MODEL slx_0b62965fec34
KIND model
CONFIG AbsTol = auto
CONFIG EnableMultiTasking = off
CONFIG FixedStep = 5e-6
CONFIG MaxStep = auto
CONFIG MinStep = auto
CONFIG RelTol = 1e-3
CONFIG SampleTimeConstraint = Unconstrained
CONFIG Solver = FixedStepDiscrete
CONFIG SolverName = FixedStepDiscrete
CONFIG StartTime = 0.0
CONFIG StopTime = 5.0
BLOCK [Reference] AC DC Converter Rectifier  REF=powerlib/Power
Electronics/Universal Bridge
  Ports = [0, 0, 0, 0, 0, 3, 2]
  SourceBlock = powerlib/Power\nElectronics/Universal Bridge
  SourceProductBaseCode = PS
  SourceProductName = Simscape Power Systems
  SourceType = Universal Bridge
BLOCK [Sum] Add
  InputSameDT = off
  Inputs = +-
  OutDataTypeStr = Inherit: Inherit via internal rule
  Ports = [2, 1]
  SaturateOnIntegerOverflow = off
BLOCK [Sum] Add1
  InputSameDT = off
  Inputs = +-
  OutDataTypeStr = Inherit: Inherit via internal rule
  Ports = [2, 1]
  SaturateOnIntegerOverflow = off
BLOCK [Sum] Add2
  InputSameDT = off
  Inputs = +-
  OutDataTypeStr = Inherit: Inherit via internal rule
  Ports = [2, 1]
  SaturateOnIntegerOverflow = off
BLOCK [Reference] Battery  REF=electricdrivelib/Extra Sources/Battery
  Ports = [0, 1, 0, 0, 0, 2]
  SourceBlock = electricdrivelib/Extra Sources/Battery
  SourceProductBaseCode = PS
  SourceProductName = Simscape Power Systems
  SourceType = Battery
BLOCK [BusSelector] Bus Selector
  OutputAsBus = off
  OutputSignals = SOC (%),Current (A),Voltage (V)
  Ports = [1, 3]
BLOCK [BusSelector] Bus Selector1
  OutputAsBus = off
  OutputSignals = V_PV,I_PV
  Ports = [1, 2]
BLOCK [Constant] Constant
  Value = 25.98
BLOCK [Constant] Constant1
  Value = 100
BLOCK [Constant] Constant2
BLOCK [Constant] Constant3
  Value = 0.5
BLOCK [Constant] Constant4
  Value = 1.2
BLOCK [Constant] Constant5
  Value = 0
BLOCK [Constant] Constant6
  Value = 0
BLOCK [Constant] Constant8
  Value = 0
BLOCK [Reference] Current Measurement1  REF=powerlib/Measurements/Current Measurement
  Ports = [0, 1, 0, 0, 0, 1, 1]
  SourceBlock = powerlib/Measurements/Current Measurement
  SourceProductBaseCode = PS
  SourceProductName = Simscape Power Systems
  SourceType = Current Measurement
  UserDataPersistent = on
BLOCK [Reference] Current PID Controller1  REF=simulink/Continuous/PID Controller
  Ports = [1, 1]
  SourceBlock = simulink/Continuous/PID Controller
  SourceProductBaseCode = SL
  SourceProductName = Simulink
  SourceType = PID 1dof
BLOCK [Reference] Current PID Controller2  REF=simulink/Continuous/PID Controller
  Ports = [1, 1]
  SourceBlock = simulink/Continuous/PID Controller
  SourceProductBaseCode = SL
  SourceProductName = Simulink
  SourceType = PID 1dof
BLOCK [Reference] Diode  REF=powerlib/Power
Electronics/Diode
  Ports = [0, 0, 0, 0, 0, 1, 1]
  SourceBlock = powerlib/Power\nElectronics/Diode
  SourceProductBaseCode = PS
  SourceProductName = Simscape Power Systems
  SourceType = Diode
BLOCK [Display] Display
  Decimation = 1
  Ports = [1]
BLOCK [Display] Display1
  Decimation = 1
  Ports = [1]
BLOCK [Display] Display2
  Decimation = 1
  Ports = [1]
BLOCK [Display] Display3
  Decimation = 1
  Ports = [1]
BLOCK [Display] Display4
  Decimation = 1
  Ports = [1]
BLOCK [Display] Display5
  Decimation = 1
  Ports = [1]
BLOCK [Display] Display6
  Decimation = 1
  Ports = [1]
BLOCK [Reference] Filter  REF=powerlib/Elements/Series RLC Branch
  Ports = [0, 0, 0, 0, 0, 1, 1]
  SourceBlock = powerlib/Elements/Series RLC Branch
  SourceProductBaseCode = PS
  SourceProductName = Simscape Power Systems
  SourceType = Series RLC Branch
BLOCK [From] From
  GotoTag = S_P
BLOCK [From] From1
  GotoTag = S_N
BLOCK [From] From10
  GotoTag = Ib_ref
BLOCK [From] From11
  GotoTag = V_bus
  TagVisibility = global
BLOCK [From] From12
  GotoTag = Ib_ref_dis
BLOCK [From] From13
  GotoTag = Bt_sg
  TagVisibility = global
BLOCK [From] From14
  GotoTag = S_boost
BLOCK [From] From15
  GotoTag = V_pv
  TagVisibility = global
BLOCK [From] From16
  GotoTag = V_bus
  TagVisibility = global
BLOCK [From] From17
  GotoTag = Irradiance
  TagVisibility = global
BLOCK [From] From18
  GotoTag = I_bus
  TagVisibility = global
BLOCK [From] From19
  GotoTag = V_Grid
  TagVisibility = global
BLOCK [From] From2
  GotoTag = I_b
  TagVisibility = global
BLOCK [From] From20
  GotoTag = P_bus
  TagVisibility = global
BLOCK [From] From21
  GotoTag = P_pv
  TagVisibility = global
BLOCK [From] From22
  GotoTag = Irradiance
  TagVisibility = global
BLOCK [From] From23
  GotoTag = Solar
  TagVisibility = global
BLOCK [From] From24
  GotoTag = Solar_v
  TagVisibility = global
BLOCK [From] From25
  GotoTag = Wind
BLOCK [From] From26
  GotoTag = Wind_V
BLOCK [From] From27
  GotoTag = Grid_V
BLOCK [From] From3
  GotoTag = SOC
  TagVisibility = global
BLOCK [From] From4
  GotoTag = I_pv
  TagVisibility = global
BLOCK [From] From5
  GotoTag = Ib_ref_ch
BLOCK [From] From6
  GotoTag = Wind_Speed
BLOCK [From] From7
  GotoTag = I_bus
  TagVisibility = global
BLOCK [From] From8
  GotoTag = V_b
  TagVisibility = global
BLOCK [From] From9
  GotoTag = V_bus
  TagVisibility = global
BLOCK [Gain] Gain
  Gain = -1
  OutDataTypeStr = Inherit: Inherit via internal rule
  ParamDataTypeStr = Inherit: Inherit via internal rule
  SaturateOnIntegerOverflow = off
BLOCK [Goto] Goto
  GotoTag = SOC
  TagVisibility = global
BLOCK [Goto] Goto1
  GotoTag = I_b
  TagVisibility = global
BLOCK [Goto] Goto10
  GotoTag = V_pv
  TagVisibility = global
BLOCK [Goto] Goto11
  GotoTag = I_pv
  TagVisibility = global
BLOCK [Goto] Goto12
  GotoTag = Irradiance
  TagVisibility = global
BLOCK [Goto] Goto13
  GotoTag = S_boost
BLOCK [Goto] Goto14
  GotoTag = V_bus
  TagVisibility = global
BLOCK [Goto] Goto15
  GotoTag = I_bus
  TagVisibility = global
BLOCK [Goto] Goto16
  GotoTag = gridsg
BLOCK [Goto] Goto17
  GotoTag = P_bus
  TagVisibility = global
BLOCK [Goto] Goto18
  GotoTag = P_pv
  TagVisibility = global
BLOCK [Goto] Goto19
  GotoTag = Wind_Speed
BLOCK [Goto] Goto2
  GotoTag = V_b
  TagVisibility = global
BLOCK [Goto] Goto20
  GotoTag = Solar
  TagVisibility = global
BLOCK [Goto] Goto21
  GotoTag = Solar_v
  TagVisibility = global
BLOCK [Goto] Goto22
  GotoTag = Wind
BLOCK [Goto] Goto23
  GotoTag = Wind_V
BLOCK [Goto] Goto24
  GotoTag = Grid_V
BLOCK [Goto] Goto3
  GotoTag = S_N
BLOCK [Goto] Goto4
  GotoTag = S_P
BLOCK [Goto] Goto5
  GotoTag = Ib_ref_ch
BLOCK [Goto] Goto6
  GotoTag = V_Grid
  TagVisibility = global
BLOCK [Goto] Goto7
  GotoTag = Ib_ref_dis
BLOCK [Goto] Goto8
  GotoTag = Ib_ref
BLOCK [Goto] Goto9
  GotoTag = Bt_sg
  TagVisibility = global
BLOCK [Reference] Ground  REF=powerlib/Elements/Ground
  Ports = [0, 0, 0, 0, 0, 1]
  SourceBlock = powerlib/Elements/Ground
  SourceProductBaseCode = PS
  SourceProductName = Simscape Power Systems
  SourceType = Ground
BLOCK [Reference] IGBT//Diode  REF=powerlib/Power
Electronics/IGBT//Diode
  Ports = [1, 1, 0, 0, 0, 1, 1]
  SourceBlock = powerlib/Power\nElectronics/IGBT//Diode
  SourceProductBaseCode = PS
  SourceProductName = Simscape Power Systems
  SourceType = IGBT/Diode
BLOCK [Reference] Ideal Switch  REF=powerlib/Power
Electronics/Ideal Switch
  Ports = [1, 0, 0, 0, 0, 1, 1]
  SourceBlock = powerlib/Power\nElectronics/Ideal Switch
  SourceProductBaseCode = PS
  SourceProductName = Simscape Power Systems
  SourceType = Ideal Switch
BLOCK [Logic] Logical Operator
  AllPortsSameDT = off
  Operator = NOT
  OutDataTypeStr = boolean
  Ports = [1, 1]
BLOCK [Reference] Mosfet  REF=powerlib/Power
Electronics/Mosfet
  Ports = [1, 0, 0, 0, 0, 1, 1]
  SourceBlock = powerlib/Power\nElectronics/Mosfet
  SourceProductBaseCode = PS
  SourceProductName = Simscape Power Systems
  SourceType = Mosfet
BLOCK [Reference] Mosfet1  REF=powerlib/Power
Electronics/Mosfet
  Ports = [1, 0, 0, 0, 0, 1, 1]
  SourceBlock = powerlib/Power\nElectronics/Mosfet
  SourceProductBaseCode = PS
  SourceProductName = Simscape Power Systems
  SourceType = Mosfet
BLOCK [Reference] PV Array  REF=re_lib/Solar/PV Array
  Ports = [2, 1, 0, 0, 0, 0, 2]
  SourceBlock = re_lib/Solar/PV Array
  SourceProductBaseCode = PS
  SourceProductName = Simscape Power Systems
  SourceType = PV array
BLOCK [Reference] PWM Generator (DC-DC)  REF=powerlib_meascontrol/Pulse & Signal
Generators/PWM Generator
(DC-DC)
  Ports = [1, 1]
  SourceBlock = powerlib_meascontrol/Pulse & Signal\nGenerators/PWM Generator\n(DC-DC)
  SourceProductBaseCode = PS
  SourceProductName = Simscape Power Systems
  SourceType = PWM Generator (DC-DC)
BLOCK [Reference] PWM Generator (DC-DC)1  REF=powerlib_meascontrol/Pulse & Signal
Generators/PWM Generator
(DC-DC)
  Ports = [1, 1]
  SourceBlock = powerlib_meascontrol/Pulse & Signal\nGenerators/PWM Generator\n(DC-DC)
  SourceProductBaseCode = PS
  SourceProductName = Simscape Power Systems
  SourceType = PWM Generator (DC-DC)
BLOCK [Product] P_bus
  InputSameDT = off
  OutDataTypeStr = Inherit: Inherit via internal rule
  Ports = [2, 1]
  RndMeth = Floor
  SaturateOnIntegerOverflow = off
BLOCK [Product] P_pv
  InputSameDT = off
  OutDataTypeStr = Inherit: Inherit via internal rule
  Ports = [2, 1]
  RndMeth = Floor
  SaturateOnIntegerOverflow = off
BLOCK [Reference] Permanent Magnet Synchronous Machine  REF=powerlib/Machines/Permanent Magnet
Synchronous Machine
  Ports = [1, 1, 0, 0, 0, 3]
  SourceBlock = powerlib/Machines/Permanent Magnet\nSynchronous Machine
  SourceProductBaseCode = PS
  SourceProductName = Simscape Power Systems
  SourceType = Permanent Magnet Synchronous Machine
BLOCK [Scope] Scope
  Floating = off
  NumInputPorts = 8
  Ports = [8]
  ScopeSpecificationString = Simulink.scopes.TimeScopeBlockCfg('CurrentConfiguration', extmgr.ConfigurationSet(extmgr.Configuration('Core','General UI',true,'FigureColor',[1 1 1]),extmgr.Configuration('Core','Source UI',true),extmgr.Configuration('Sources','WiredSimulink',true,'DataLogging',true),extmgr.Configuration('Visuals','Time Domain',true,'SerializedDisplays',{struct('MinYLimReal','-248.28438','MaxYLimReal','248.28537'...<+7768ch>
BLOCK [Reference] Series RLC Branch  REF=powerlib/Elements/Series RLC Branch
  Ports = [0, 0, 0, 0, 0, 1, 1]
  SourceBlock = powerlib/Elements/Series RLC Branch
  SourceProductBaseCode = PS
  SourceProductName = Simscape Power Systems
  SourceType = Series RLC Branch
BLOCK [Reference] Series RLC Branch1  REF=powerlib/Elements/Series RLC Branch
  Ports = [0, 0, 0, 0, 0, 1, 1]
  SourceBlock = powerlib/Elements/Series RLC Branch
  SourceProductBaseCode = PS
  SourceProductName = Simscape Power Systems
  SourceType = Series RLC Branch
BLOCK [Reference] Series RLC Branch2  REF=powerlib/Elements/Series RLC Branch
  Ports = [0, 0, 0, 0, 0, 1, 1]
  SourceBlock = powerlib/Elements/Series RLC Branch
  SourceProductBaseCode = PS
  SourceProductName = Simscape Power Systems
  SourceType = Series RLC Branch
BLOCK [Reference] Series RLC Branch3  REF=powerlib/Elements/Series RLC Branch
  Ports = [0, 0, 0, 0, 0, 1, 1]
  SourceBlock = powerlib/Elements/Series RLC Branch
  SourceProductBaseCode = PS
  SourceProductName = Simscape Power Systems
  SourceType = Series RLC Branch
BLOCK [Reference] Series RLC Branch4  REF=powerlib/Elements/Series RLC Branch
  Ports = [0, 0, 0, 0, 0, 1, 1]
  SourceBlock = powerlib/Elements/Series RLC Branch
  SourceProductBaseCode = PS
  SourceProductName = Simscape Power Systems
  SourceType = Series RLC Branch
BLOCK [Reference] Series RLC Branch5  REF=powerlib/Elements/Series RLC Branch
  Ports = [0, 0, 0, 0, 0, 1, 1]
  SourceBlock = powerlib/Elements/Series RLC Branch
  SourceProductBaseCode = PS
  SourceProductName = Simscape Power Systems
  SourceType = Series RLC Branch
BLOCK [Reference] Series RLC Branch6  REF=powerlib/Elements/Series RLC Branch
  Ports = [0, 0, 0, 0, 0, 1, 1]
  SourceBlock = powerlib/Elements/Series RLC Branch
  SourceProductBaseCode = PS
  SourceProductName = Simscape Power Systems
  SourceType = Series RLC Branch
BLOCK [Reference] Series RLC Branch7  REF=powerlib/Elements/Series RLC Branch
  Ports = [0, 0, 0, 0, 0, 1, 1]
  SourceBlock = powerlib/Elements/Series RLC Branch
  SourceProductBaseCode = PS
  SourceProductName = Simscape Power Systems
  SourceType = Series RLC Branch
BLOCK [Reference] Series RLC Branch8  REF=powerlib/Elements/Series RLC Branch
  Ports = [0, 0, 0, 0, 0, 1, 1]
  SourceBlock = powerlib/Elements/Series RLC Branch
  SourceProductBaseCode = PS
  SourceProductName = Simscape Power Systems
  SourceType = Series RLC Branch
BLOCK [Reference] Series RLC Branch9  REF=powerlib/Elements/Series RLC Branch
  Ports = [0, 0, 0, 0, 0, 1, 1]
  SourceBlock = powerlib/Elements/Series RLC Branch
  SourceProductBaseCode = PS
  SourceProductName = Simscape Power Systems
  SourceType = Series RLC Branch
BLOCK [Step] Step
  After = 0
  Before = 1000
  SampleTime = 0
  Time = 3
BLOCK [Step] Step1
  After = 0
  Before = 12
  SampleTime = 0
  Time = 4
BLOCK [Step] Step2
  After = 0
  Before = 1
  SampleTime = 0
  Time = 1.5
BLOCK [Sum] Sum
  IconShape = round
  InputSameDT = off
  Inputs = |++
  OutDataTypeStr = Inherit: Inherit via internal rule
  Ports = [2, 1]
  SaturateOnIntegerOverflow = off
BLOCK [Switch] Switch
  Criteria = u2 > Threshold
  InputSameDT = off
  SaturateOnIntegerOverflow = off
BLOCK [Switch] Switch1
  Criteria = u2 > Threshold
  InputSameDT = off
  SaturateOnIntegerOverflow = off
BLOCK [Switch] Switch2
  Criteria = u2 ~= 0
  InputSameDT = off
  SaturateOnIntegerOverflow = off
BLOCK [Constant] Temp
  Value = 25
BLOCK [Reference] Three-Phase Breaker  REF=powerlib/Elements/Three-Phase Breaker
  Ports = [1, 0, 0, 0, 0, 3, 3]
  SourceBlock = powerlib/Elements/Three-Phase Breaker
  SourceProductBaseCode = PS
  SourceProductName = Simscape Power Systems
  SourceType = Three-Phase Breaker
BLOCK [Reference] Three-Phase Source 11kv  REF=powerlib/Electrical
Sources/Three-Phase Source
  Ports = [0, 0, 0, 0, 0, 0, 3]
  SourceBlock = powerlib/Electrical\nSources/Three-Phase Source
  SourceProductBaseCode = PS
  SourceProductName = Simscape Power Systems
  SourceType = Three-Phase Source
BLOCK [Reference] Three-Phase Transformer (Two Windings) 11kv//250v 100KVA  REF=powerlib/Elements/Three-Phase
Transformer
(Two Windings)
  Ports = [0, 0, 0, 0, 0, 3, 4]
  SourceBlock = powerlib/Elements/Three-Phase\nTransformer\n(Two Windings)
  SourceProductBaseCode = PS
  SourceProductName = Simscape Power Systems
  SourceType = Three-Phase Transformer (Two Windings)
BLOCK [Reference] Three-Phase V-I Measurement  REF=powerlib/Measurements/Three-Phase
V-I Measurement
  Ports = [0, 0, 0, 0, 0, 3, 3]
  SourceBlock = powerlib/Measurements/Three-Phase\nV-I Measurement
  SourceProductBaseCode = PS
  SourceProductName = Simscape Power Systems
  SourceType = Three-Phase VI Measurement
BLOCK [Reference] Three-Phase V-I Measurement1  REF=powerlib/Measurements/Three-Phase
V-I Measurement
  Ports = [0, 1, 0, 0, 0, 3, 3]
  SourceBlock = powerlib/Measurements/Three-Phase\nV-I Measurement
  SourceProductBaseCode = PS
  SourceProductName = Simscape Power Systems
  SourceType = Three-Phase VI Measurement
BLOCK [Reference] Universal Bridge1  REF=powerlib/Power
Electronics/Universal Bridge
  Ports = [0, 0, 0, 0, 0, 3, 2]
  SourceBlock = powerlib/Power\nElectronics/Universal Bridge
  SourceProductBaseCode = PS
  SourceProductName = Simscape Power Systems
  SourceType = Universal Bridge
BLOCK [Reference] Voltage Measurement2  REF=powerlib/Measurements/Voltage Measurement
  Ports = [0, 1, 0, 0, 0, 2]
  SourceBlock = powerlib/Measurements/Voltage Measurement
  SourceProductBaseCode = PS
  SourceProductName = Simscape Power Systems
  SourceType = Voltage Measurement
  UserDataPersistent = on
BLOCK [Reference] Voltage PID Controller  REF=simulink/Continuous/PID Controller
  Ports = [1, 1]
  SourceBlock = simulink/Continuous/PID Controller
  SourceProductBaseCode = SL
  SourceProductName = Simulink
  SourceType = PID 1dof
BLOCK [Reference] Wind Turbine  REF=re_lib/Wind Generation/Wind Turbine
  Ports = [3, 1]
  SourceBlock = re_lib/Wind Generation/Wind Turbine
  SourceProductBaseCode = PS
  SourceProductName = Simscape Power Systems
  SourceType = Wind Turbine
BLOCK [From] grid
  GotoTag = gridsg
BLOCK [From] grid1
  GotoTag = gridsg
BLOCK [Reference] powergui  REF=powerlib/powergui
  Ports = []
  Priority = 1
  SourceBlock = powerlib/powergui
  SourceProductBaseCode = PS
  SourceProductName = Simscape Power Systems
  SourceType = PSB option menu block
ANNOTATION (root): MEASUREMENT BLOCK
ANNOTATION (root): DESIGNED BY: Er.DANISH NAZIR SHAH <email> 9018561666
ANNOTATION (root): CONTROL BLOCK
ANNOTATION (root): DESIGN OF DC MICROGRID
ANNOTATION (root): DC BUS
ANNOTATION (root): GRID
ANNOTATION (root): SOLAR
ANNOTATION (root): WIND
ANNOTATION (root): PCC
ANNOTATION (root): LOAD 10kW
ANNOTATION (root): 12 KW SOLAR PANNEL
ANNOTATION (root): 24V 100AH BATTERY BANK
ANNOTATION (root): 11kW Wind Turbine
ANNOTATION (root): GRID CONNECTION
ANNOTATION (root): INPUT BLOCK
LINE Add1:1 -> Current PID Controller1:1
LINE Add2:1 -> Current PID Controller2:1
LINE Add:1 -> Voltage PID Controller:1
LINE Battery:1 -> Bus Selector:1
LINE Bus Selector1:1 -> Goto10:1
LINE Bus Selector1:2 -> Goto11:1
LINE Bus Selector:1 -> Goto:1
LINE Bus Selector:2 -> Goto1:1
LINE Bus Selector:3 -> Goto2:1
LINE Constant1:1 -> Add2:1
NET Constant2:1 -> Goto9:1, Ideal Switch:1
LINE Constant3:1 -> PWM Generator (DC-DC)1:1
LINE Constant4:1 -> Wind Turbine:1
LINE Constant5:1 -> Wind Turbine:2
LINE Constant6:1 -> Switch1:1
LINE Constant8:1 -> Switch2:1
LINE Constant:1 -> Add1:1
NET Current Measurement1:1 -> Display5:1, Goto15:1
LINE Current PID Controller1:1 -> Gain:1
LINE Current PID Controller2:1 -> Goto7:1
LINE From10:1 -> Add:2
NET From11:1 -> Display1:1, Scope:4
LINE From12:1 -> Switch:3
LINE From13:1 -> Switch:2
LINE From14:1 -> IGBT//Diode:1
LINE From15:1 -> P_pv:1
LINE From16:1 -> P_bus:2
LINE From17:1 -> Scope:2
LINE From18:1 -> P_bus:1
NET From19:1 -> Display:1, Scope:1
LINE From1:1 -> Mosfet:1
NET From20:1 -> Display2:1, Scope:5
NET From21:1 -> Display3:1, Scope:6
LINE From22:1 -> Sum:2
NET From23:1 -> Goto12:1, PV Array:1
LINE From24:1 -> Switch1:3
NET From25:1 -> Goto19:1, Wind Turbine:3
LINE From26:1 -> Switch2:3
NET From27:1 -> Goto16:1, Three-Phase Breaker:1
LINE From2:1 -> Add:1
LINE From3:1 -> Scope:7
LINE From4:1 -> P_pv:2
LINE From5:1 -> Switch:1
LINE From6:1 -> Scope:3
NET From7:1 -> Display6:1, Scope:8
LINE From8:1 -> Add1:2
LINE From9:1 -> Add2:2
LINE From:1 -> Mosfet1:1
LINE Gain:1 -> Goto5:1
LINE Logical Operator:1 -> Goto3:1
LINE PV Array:1 -> Bus Selector1:1
LINE PWM Generator (DC-DC)1:1 -> Goto13:1
NET PWM Generator (DC-DC):1 -> Goto4:1, Logical Operator:1
LINE P_bus:1 -> Goto17:1
LINE P_pv:1 -> Goto18:1
LINE Step1:1 -> Goto23:1
LINE Step2:1 -> Goto24:1
LINE Step:1 -> Goto21:1
LINE Sum:1 -> Switch2:2
LINE Switch1:1 -> Goto20:1
LINE Switch2:1 -> Goto22:1
LINE Switch:1 -> Goto8:1
LINE Temp:1 -> PV Array:2
LINE Three-Phase V-I Measurement1:1 -> Goto6:1
NET Voltage Measurement2:1 -> Display4:1, Goto14:1
LINE Voltage PID Controller:1 -> PWM Generator (DC-DC):1
LINE Wind Turbine:1 -> Permanent Magnet Synchronous Machine:1
LINE grid1:1 -> Sum:1
LINE grid:1 -> Switch1:2
PLINE AC DC Converter Rectifier:LConn1 -- Three-Phase V-I Measurement1:RConn1
PLINE AC DC Converter Rectifier:LConn2 -- Three-Phase V-I Measurement1:RConn2
PLINE AC DC Converter Rectifier:LConn3 -- Three-Phase V-I Measurement1:RConn3
PLINE AC DC Converter Rectifier:RConn1 -- Filter:LConn1
PNET net1: AC DC Converter Rectifier:RConn2 -- Battery:LConn2 -- IGBT//Diode:RConn1 -- Mosfet:RConn1 -- PV Array:RConn2 -- Series RLC Branch1:RConn1 -- Series RLC Branch2:RConn1 -- Series RLC Branch3:RConn1 -- Series RLC Branch5:RConn1 -- Series RLC Branch6:RConn1 -- Series RLC Branch7:RConn1 -- Series RLC Branch8:RConn1 -- Universal Bridge1:RConn2 -- Voltage Measurement2:LConn2
PLINE Battery:LConn1 -- Series RLC Branch:RConn1
PNET net2: Current Measurement1:LConn1 -- Diode:RConn1 -- Filter:RConn1 -- Ideal Switch:RConn1 -- Series RLC Branch5:LConn1 -- Universal Bridge1:RConn1
PNET net3: Current Measurement1:RConn1 -- Series RLC Branch2:LConn1 -- Series RLC Branch6:LConn1 -- Series RLC Branch7:LConn1 -- Series RLC Branch8:LConn1 -- Voltage Measurement2:LConn1
PNET net4: Diode:LConn1 -- IGBT//Diode:LConn1 -- Series RLC Branch4:RConn1
PLINE Ground:LConn1 -- Series RLC Branch9:RConn1
PNET net5: Ideal Switch:LConn1 -- Mosfet1:LConn1 -- Series RLC Branch1:LConn1
PNET net6: Mosfet1:RConn1 -- Mosfet:LConn1 -- Series RLC Branch:LConn1
PNET net7: PV Array:RConn1 -- Series RLC Branch3:LConn1 -- Series RLC Branch4:LConn1
PLINE Permanent Magnet Synchronous Machine:LConn1 -- Universal Bridge1:LConn1
PLINE Permanent Magnet Synchronous Machine:LConn2 -- Universal Bridge1:LConn2
PLINE Permanent Magnet Synchronous Machine:LConn3 -- Universal Bridge1:LConn3
PLINE Series RLC Branch9:LConn1 -- Three-Phase Transformer (Two Windings) 11kv//250v 100KVA:RConn4
PLINE Three-Phase Breaker:LConn1 -- Three-Phase V-I Measurement:RConn1
PLINE Three-Phase Breaker:LConn2 -- Three-Phase V-I Measurement:RConn2
PLINE Three-Phase Breaker:LConn3 -- Three-Phase V-I Measurement:RConn3
PLINE Three-Phase Breaker:RConn1 -- Three-Phase Transformer (Two Windings) 11kv//250v 100KVA:LConn1
PLINE Three-Phase Breaker:RConn2 -- Three-Phase Transformer (Two Windings) 11kv//250v 100KVA:LConn2
PLINE Three-Phase Breaker:RConn3 -- Three-Phase Transformer (Two Windings) 11kv//250v 100KVA:LConn3
PLINE Three-Phase Source 11kv:RConn1 -- Three-Phase V-I Measurement:LConn1
PLINE Three-Phase Source 11kv:RConn2 -- Three-Phase V-I Measurement:LConn2
PLINE Three-Phase Source 11kv:RConn3 -- Three-Phase V-I Measurement:LConn3
PLINE Three-Phase Transformer (Two Windings) 11kv//250v 100KVA:RConn1 -- Three-Phase V-I Measurement1:LConn1
PLINE Three-Phase Transformer (Two Windings) 11kv//250v 100KVA:RConn2 -- Three-Phase V-I Measurement1:LConn2
PLINE Three-Phase Transformer (Two Windings) 11kv//250v 100KVA:RConn3 -- Three-Phase V-I Measurement1:LConn3
note: NET lines group one-source signal fan-out (src -> all destinations, sorted); 1:1 wires keep LINE; PNET lines group multi-terminal physical nets as a canonical sorted terminal list (undirected conserving connections); 2-terminal nets keep the pairwise PLINE form
